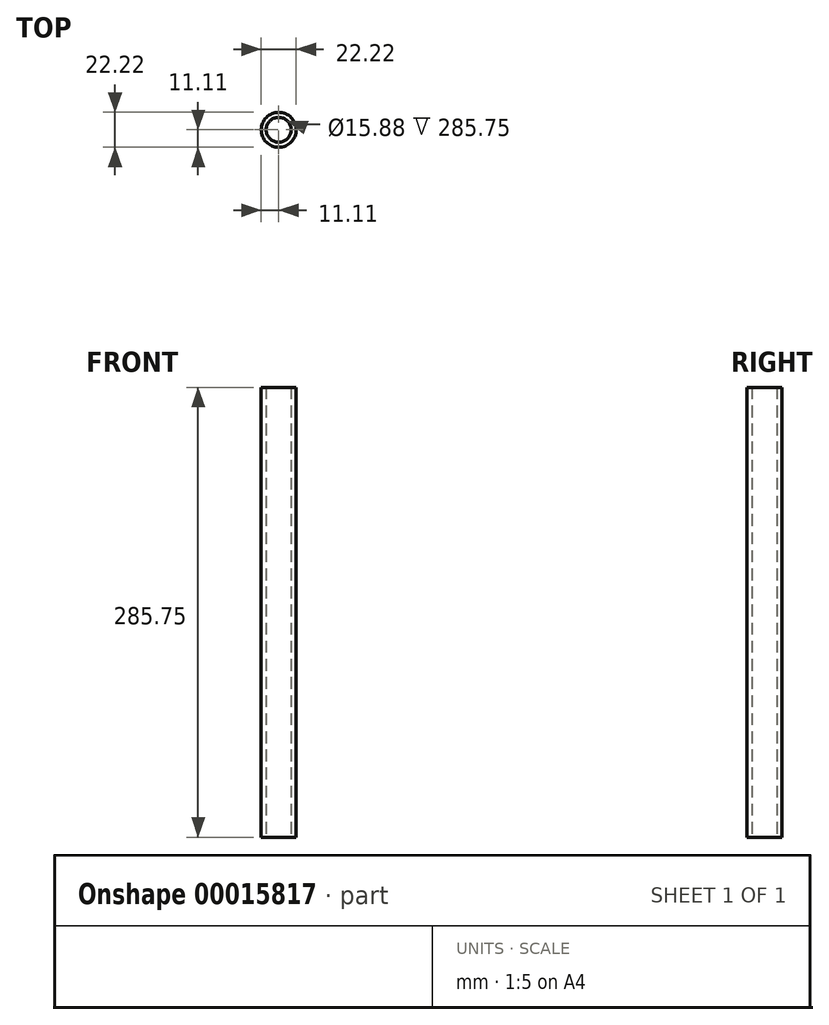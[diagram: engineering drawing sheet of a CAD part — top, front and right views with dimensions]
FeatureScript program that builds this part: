
annotation { "Feature Type Name" : "Feature", "Feature Type Description" : "" }
export const myFeature = defineFeature(function(context is Context, id is Id, definition is map)
    precondition{}
    {
        {
            var Q0;
            Q0=qCreatedBy(makeId("Top.planeOp"),FACE);
            var sketch = newSketch(context, id + "F0", { "sketchPlane" : qUnion([Q0])});
            skCircle(sketch, "E0", {"center": v(0, 0) * mm, "radius": 7.94 * mm});
            skCircle(sketch, "E1", {"center": v(0, 0) * mm, "radius": 11.11 * mm});
            skSolve(sketch);
        }
        {
            var Q0;
            Q0=qSketchRegion(id+"F0",true);
            extrude(context, id + "F1", {"entities" : qUnion([Q0]), "depth" : 285.75 * mm});
        }
    });
